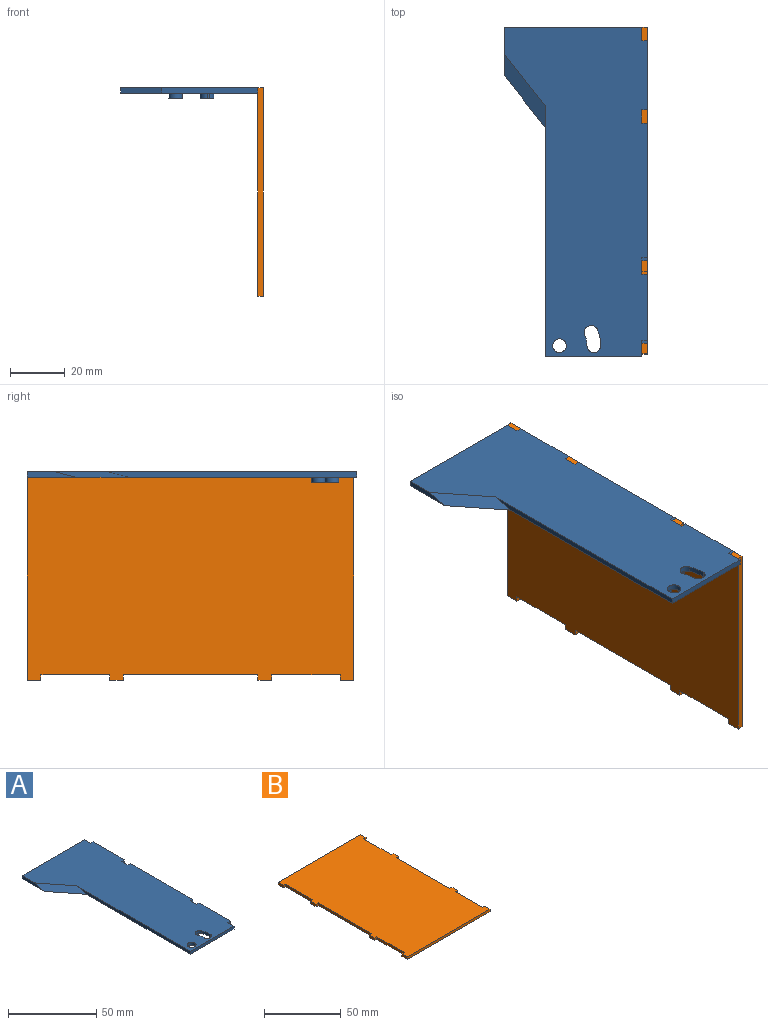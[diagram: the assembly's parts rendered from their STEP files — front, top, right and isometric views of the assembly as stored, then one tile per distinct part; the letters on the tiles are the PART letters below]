
ASSEMBLY  parts=2 mates=1
PART A: 30 faces, bbox 52x120x4 mm
  f0: plane 120x52mm, normal (0,0,1), area 4627.1mm2, adj f2,f3,f4,f5,f6,f7,f8,f9
  f1: plane 120x52mm, normal (0,0,-1), area 4704.7mm2, adj f2,f3,f4,f5,f6,f7,f8,f9
  f2: plane 91.07x2mm, normal (-1,0,0), area 174.3mm2, adj f0,f1,f3,f29
  f3: plane 35x2mm, normal (0,-1,0), area 70mm2, adj f0,f1,f2,f4
  f4: plane 5x2mm, normal (1,0,0), area 10mm2, adj f0,f1,f3,f5
  f5: plane 2x2mm, normal (0,-1,0), area 4mm2, adj f0,f1,f4,f6
  f6: plane 25x2mm, normal (1,0,0), area 50mm2, adj f0,f1,f5,f7
  f7: plane 2x2mm, normal (0,1,0), area 4mm2, adj f0,f1,f6,f8
  f8: plane 5x2mm, normal (1,0,0), area 10mm2, adj f0,f1,f7,f9
  f9: plane 2x2mm, normal (0,-1,0), area 4mm2, adj f0,f1,f8,f10
  f10: plane 50x2mm, normal (1,0,0), area 100mm2, adj f0,f1,f9,f11
  f11: plane 2x2mm, normal (0,1,0), area 4mm2, adj f0,f1,f10,f12
  f12: plane 5x2mm, normal (1,0,0), area 10mm2, adj f0,f1,f11,f13
  f13: plane 2x2mm, normal (0,-1,0), area 4mm2, adj f0,f1,f12,f14
  f14: plane 25x2mm, normal (1,0,0), area 50mm2, adj f0,f1,f13,f15
  f15: plane 2x2mm, normal (0,1,0), area 4mm2, adj f0,f1,f14,f16
  f16: plane 5x2mm, normal (1,0,0), area 10mm2, adj f0,f1,f15,f17
  f17: plane 50x2mm, normal (0,1,0), area 100mm2, adj f0,f1,f16,f18
  f18: plane 17.72x2mm, normal (-1,0,0), area 27.7mm2, adj f0,f1,f17,f29
  f19: cylinder r=2.5mm len=5mm, axis (0,0,1), area 31.4mm2, adj f1,f20
  f20: plane 5x5mm, normal (0,0,-1), area 19.6mm2, adj f19
  f21: cylinder r=2.5mm len=5mm, axis (0,0,1), area 30.6mm2, adj f1,f22,f23
  f22: cylinder r=2.5mm len=2mm, axis (0,0,1), area 0.8mm2, adj f1,f21,f23
  f23: plane 5x5mm, normal (0,0,-1), area 19.6mm2, adj f21,f22
  f24: cylinder r=10mm len=3.91mm, axis (0,0,-1), area 8mm2, adj f0,f1,f25,f27
  f25: cylinder r=2.5mm len=5mm, axis (0,0,-1), area 15.7mm2, adj f0,f1,f24,f26
  f26: cylinder r=15mm len=5.86mm, axis (0,0,-1), area 12mm2, adj f0,f1,f25,f27
  f27: cylinder r=2.5mm len=4.8mm, axis (0,0,-1), area 15.7mm2, adj f0,f1,f24,f26
  f28: cylinder r=2.5mm len=5mm, axis (0,0,-1), area 31.4mm2, adj f0,f1
  f29: plane 26.79x15mm, normal (-0.3,-0.24,0.92), area 126.5mm2, adj f0,f1,f2,f18
PART B: 30 faces, bbox 76x119x2 mm
  f0: plane 2x2mm, normal (0,1,0), area 4mm2, adj f1,f27,f28,f29
  f1: plane 49x2mm, normal (1,0,0), area 98mm2, adj f0,f2,f28,f29
  f2: plane 2x2mm, normal (0,-1,0), area 4mm2, adj f1,f3,f28,f29
  f3: plane 5x2mm, normal (1,0,0), area 10mm2, adj f2,f4,f28,f29
  f4: plane 2x2mm, normal (0,1,0), area 4mm2, adj f3,f5,f28,f29
  f5: plane 25x2mm, normal (1,0,0), area 50mm2, adj f4,f6,f28,f29
  f6: plane 2x2mm, normal (0,-1,0), area 4mm2, adj f5,f7,f28,f29
  f7: plane 5x2mm, normal (1,0,0), area 10mm2, adj f6,f8,f28,f29
  f8: plane 76x2mm, normal (0,1,0), area 152mm2, adj f7,f9,f28,f29
  f9: plane 5x2mm, normal (-1,0,0), area 10mm2, adj f8,f10,f28,f29
  f10: plane 2x2mm, normal (0,-1,0), area 4mm2, adj f9,f11,f28,f29
  f11: plane 25x2mm, normal (-1,0,0), area 50mm2, adj f10,f12,f28,f29
  f12: plane 2x2mm, normal (0,1,0), area 4mm2, adj f11,f13,f28,f29
  f13: plane 5x2mm, normal (-1,0,0), area 10mm2, adj f12,f14,f28,f29
  f14: plane 2x2mm, normal (0,-1,0), area 4mm2, adj f13,f15,f28,f29
  f15: plane 49x2mm, normal (-1,0,0), area 98mm2, adj f14,f16,f28,f29
  f16: plane 2x2mm, normal (0,1,0), area 4mm2, adj f15,f17,f28,f29
  f17: plane 5x2mm, normal (-1,0,0), area 10mm2, adj f16,f18,f28,f29
  f18: plane 2x2mm, normal (0,-1,0), area 4mm2, adj f17,f19,f28,f29
  f19: plane 25x2mm, normal (-1,0,0), area 50mm2, adj f18,f20,f28,f29
  f20: plane 2x2mm, normal (0,1,0), area 4mm2, adj f19,f21,f28,f29
  f21: plane 5x2mm, normal (-1,0,0), area 10mm2, adj f20,f22,f28,f29
  f22: plane 76x2mm, normal (0,-1,0), area 152mm2, adj f21,f23,f28,f29
  f23: plane 5x2mm, normal (1,0,0), area 10mm2, adj f22,f24,f28,f29
  f24: plane 2x2mm, normal (0,1,0), area 4mm2, adj f23,f25,f28,f29
  f25: plane 25x2mm, normal (1,0,0), area 50mm2, adj f24,f26,f28,f29
  f26: plane 2x2mm, normal (0,-1,0), area 4mm2, adj f25,f27,f28,f29
  f27: plane 5x2mm, normal (1,0,0), area 10mm2, adj f0,f26,f28,f29
  f28: plane 119x76mm, normal (0,0,1), area 8648mm2, adj f0,f1,f2,f3,f4,f5,f6,f7
  f29: plane 119x76mm, normal (0,0,-1), area 8648mm2, adj f0,f1,f2,f3,f4,f5,f6,f7
PLACE A t=(-11.3,-56.13,0)mm
PLACE B rot(axis=(0,1,0),90deg) t=(18.7,-13.34,-35.18)mm
MATE fastened B.f29 <-> A.f16  axis (-1,0,0) through (18.7,54.87,2)mm
